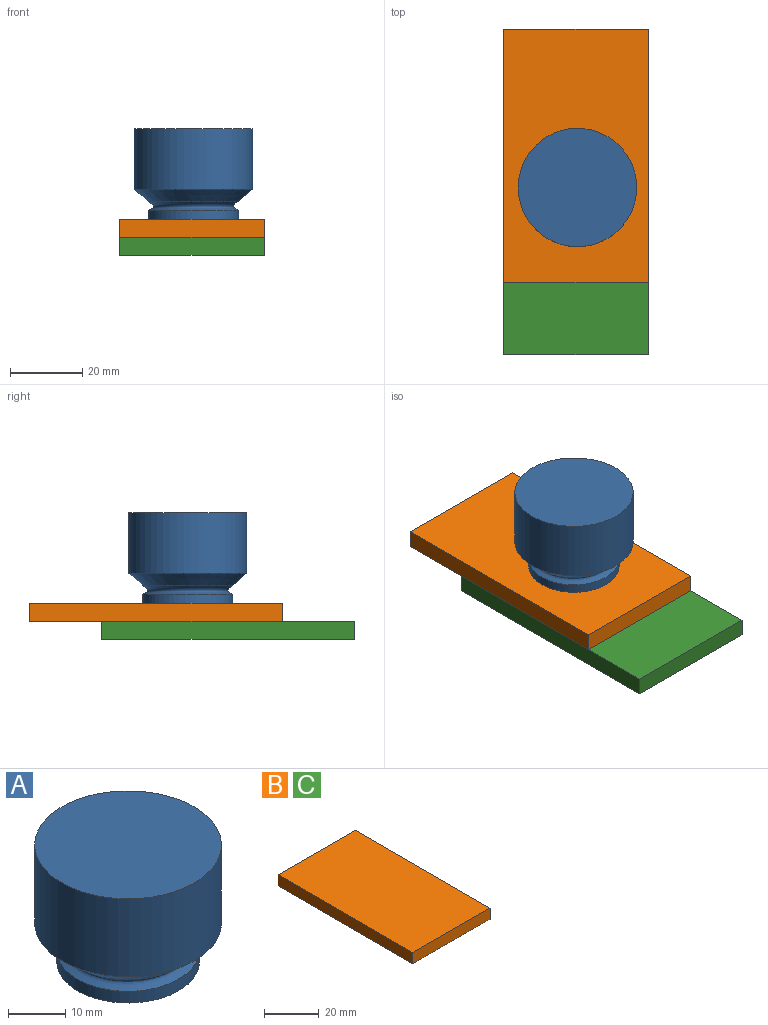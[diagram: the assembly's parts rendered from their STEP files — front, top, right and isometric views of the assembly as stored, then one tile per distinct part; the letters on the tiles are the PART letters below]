
ASSEMBLY  parts=3 mates=1
PART A: 6 faces, bbox 32.8x32.8x25.1 mm
  f0: cylinder r=16.39mm len=32.78mm, axis (0,0,1), area 1725.2mm2, adj f1,f5
  f1: plane 32.78x32.78mm, normal (0,0,1), area 844mm2, adj f0
  f2: plane 25x25mm, normal (0,0,-1), area 490.9mm2, adj f3
  f3: cylinder r=12.5mm len=25mm, axis (0,0,1), area 196.3mm2, adj f2,f4
  f4: revolved ~25.03x25.03mm, area 296.1mm2, adj f3,f5
  f5: cone r=12.51mm half-angle=49.3deg, axis (0,0,1), area 464.4mm2, adj f0,f4
PART B: 6 faces, bbox 40x70x5 mm
  f0: plane 70x5mm, normal (-1,0,0), area 350mm2, adj f1,f3,f4,f5
  f1: plane 40x5mm, normal (0,-1,0), area 200mm2, adj f0,f2,f4,f5
  f2: plane 70x5mm, normal (1,0,0), area 350mm2, adj f1,f3,f4,f5
  f3: plane 40x5mm, normal (0,1,0), area 200mm2, adj f0,f2,f4,f5
  f4: plane 70x40mm, normal (0,0,1), area 2800mm2, adj f0,f1,f2,f3
  f5: plane 70x40mm, normal (0,0,-1), area 2800mm2, adj f0,f1,f2,f3
PART C: same geometry as B
PLACE A t=(12.59,20.5,22.64)mm
PLACE B t=(-7.81,-5.7,17.64)mm
PLACE C t=(-7.81,-25.7,12.64)mm
MATE planar A.f5 <-> B.f4  axis (0,0,-1) through (12.59,20.5,22.64)mm
